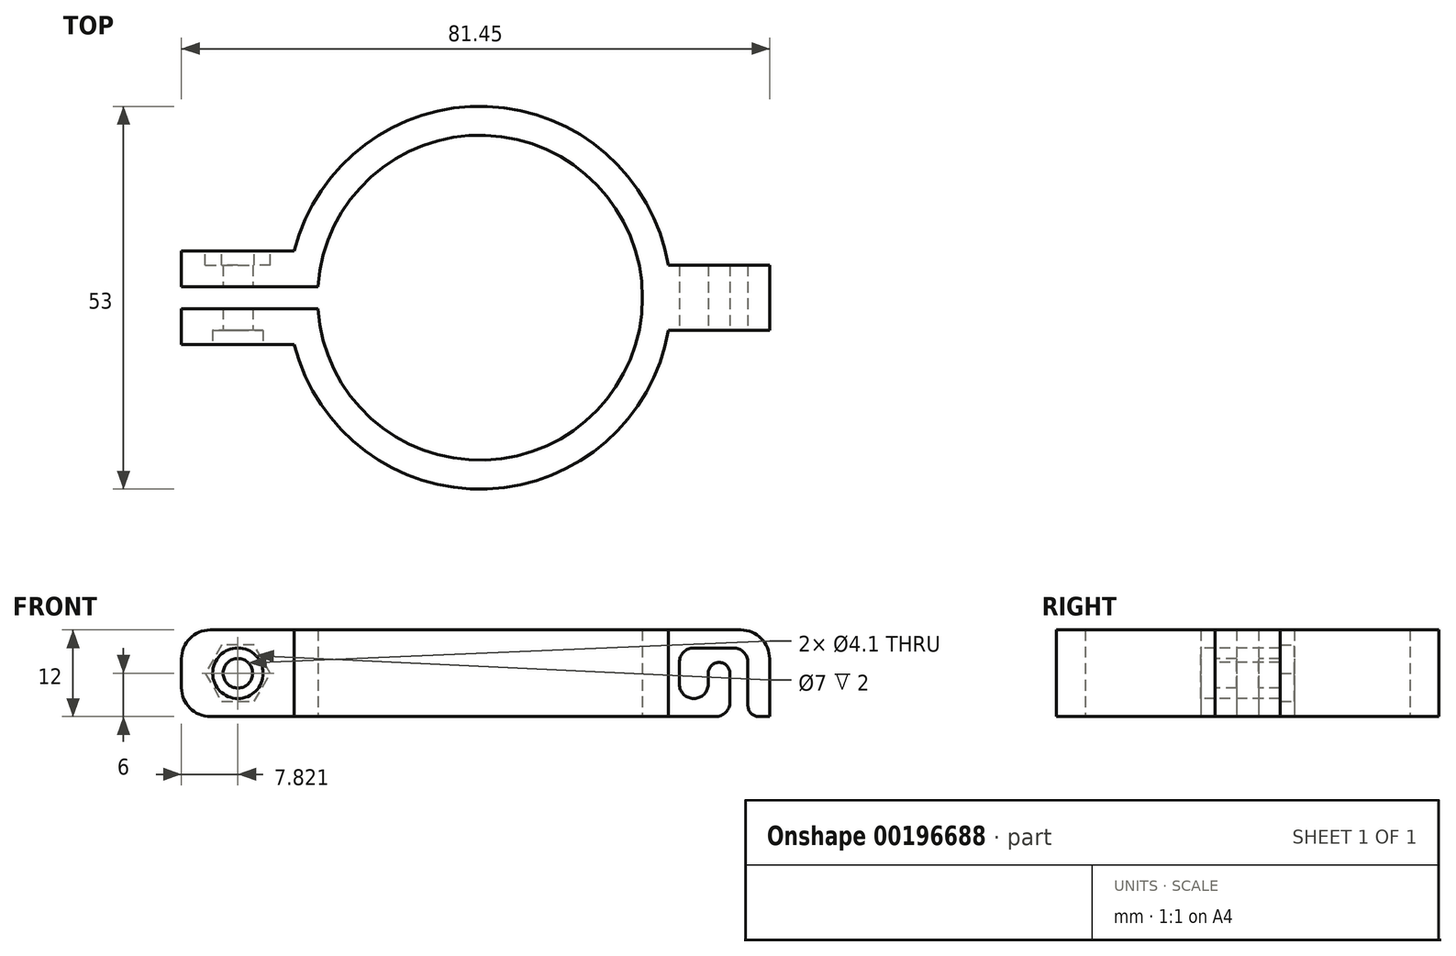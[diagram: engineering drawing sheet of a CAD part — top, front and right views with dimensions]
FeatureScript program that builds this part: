
annotation { "Feature Type Name" : "Feature", "Feature Type Description" : "" }
export const myFeature = defineFeature(function(context is Context, id is Id, definition is map)
    precondition{}
    {
        {
            var Q0;
            Q0=qCreatedBy(makeId("Top.planeOp"),FACE);
            var sketch = newSketch(context, id + "F0", { "sketchPlane" : qUnion([Q0])});
            skArc(sketch, "E0", {"start": v(-22.45, -1.5) * mm, "mid": v(22.5, 0) * mm, "end": v(-22.45, 1.5) * mm});
            skArc(sketch, "E1.0", {"start": v(-25.7, -6.5) * mm, "mid": v(1.02, -26.48) * mm, "end": v(26.12, -4.5) * mm});
            skLineSegment(sketch, "E2.top", {"start": v(-25.7, -6.5) * mm, "end": v(-41.33, -6.5) * mm});
            skLineSegment(sketch, "E2.right", {"start": v(-41.33, 6.5) * mm, "end": v(-41.33, 1.5) * mm});
            skLineSegment(sketch, "E3.MirrorCS", {"start": v(40.12, 4.5) * mm, "end": v(40.12, -4.5) * mm});
            skLineSegment(sketch, "E4", {"start": v(26.12, 4.5) * mm, "end": v(40.12, 4.5) * mm});
            skLineSegment(sketch, "E5", {"start": v(26.12, -4.5) * mm, "end": v(40.12, -4.5) * mm});
            skLineSegment(sketch, "E6", {"start": v(-22.45, 1.5) * mm, "end": v(-41.33, 1.5) * mm});
            skLineSegment(sketch, "E7", {"start": v(-22.45, -1.5) * mm, "end": v(-41.33, -1.5) * mm});
            skLineSegment(sketch, "E8.trimOffspring", {"start": v(-41.33, -1.5) * mm, "end": v(-41.33, -6.5) * mm});
            skLineSegment(sketch, "E9.trimOffspring", {"start": v(-25.7, 6.5) * mm, "end": v(-41.33, 6.5) * mm});
            skArc(sketch, "E10.trimOffspring", {"start": v(26.12, 4.5) * mm, "mid": v(1.02, 26.48) * mm, "end": v(-25.7, 6.5) * mm});
            skPoint(sketch, "E11", {"position": v(40.12, 0) * mm});
            skLineSegment(sketch, "E12", {"start": v(-65.67, 0) * mm, "end": v(55.66, 0) * mm, "construction": true});
            skSolve(sketch);
        }
        {
            var Q0;
            Q0=makeQuery(id+"F0.imprint","IMPRINT",FACE,{"disambiguationData":[TD([[makeQuery(id+"F0.imprint","IMPRINT",EDGE,{"derivedFrom":sQuery(id+"F0.wireOp",EDGE,"E0")}),-1.0]])]});
            extrude(context, id + "F1", {"entities" : qUnion([Q0]), "endBound" : BoundingType.SYMMETRIC, "depth" : 12 * mm});
        }
        {
            var Q0;
            Q0=makeQuery(id+"F1.opExtrude","SWEPT_FACE",FACE,{"disambiguationData":[OSD([sQuery(id+"F0.wireOp",EDGE,"E2.top")])]});
            var sketch = newSketch(context, id + "F2", { "sketchPlane" : qUnion([Q0])});
            skCircle(sketch, "E13", {"center": v(-33.5, 0) * mm, "radius": 2.05 * mm});
            skPoint(sketch, "E13.centerSnap0", {"position": v(-33.5, 6) * mm});
            skCircle(sketch, "E14", {"center": v(-33.5, 0) * mm, "radius": 3.5 * mm});
            skSolve(sketch);
        }
        {
            var Q0;
            Q0=makeQuery(id+"F1.opExtrude","SWEPT_FACE",FACE,{"disambiguationData":[OSD([sQuery(id+"F0.wireOp",EDGE,"E9.trimOffspring")])]});
            var sketch = newSketch(context, id + "F3", { "sketchPlane" : qUnion([Q0])});
            skCircle(sketch, "E15.cCircle", {"center": v(33.5, 0) * mm, "radius": 3.9 * mm, "construction": true});
            skPoint(sketch, "E15.cCircle.centerSnap0", {"position": v(33.5, -6) * mm});
            skPoint(sketch, "E15.cCircle.centerSnap1", {"position": v(41.33, 0) * mm});
            skLineSegment(sketch, "E15.0", {"start": v(35.76, -3.9) * mm, "end": v(31.26, -3.9) * mm});
            skLineSegment(sketch, "E15.1", {"start": v(31.26, -3.9) * mm, "end": v(29, 0) * mm});
            skLineSegment(sketch, "E15.2", {"start": v(29, 0) * mm, "end": v(31.26, 3.9) * mm});
            skLineSegment(sketch, "E15.3", {"start": v(31.26, 3.9) * mm, "end": v(35.76, 3.9) * mm});
            skLineSegment(sketch, "E15.4", {"start": v(35.76, 3.9) * mm, "end": v(38, 0) * mm});
            skLineSegment(sketch, "E15.5", {"start": v(38, 0) * mm, "end": v(35.76, -3.9) * mm});
            skPoint(sketch, "E15.0.midPoint", {"position": v(33.5, -3.9) * mm});
            skSolve(sketch);
        }
        {
            var Q0;
            Q0=makeQuery(id+"F1.opExtrude","SWEPT_FACE",FACE,{"disambiguationData":[OSD([sQuery(id+"F0.wireOp",EDGE,"E5")])]});
            var sketch = newSketch(context, id + "F4", { "sketchPlane" : qUnion([Q0])});
            skLineSegment(sketch, "E16", {"start": v(37.12, -4.5) * mm, "end": v(37.12, 1.5) * mm});
            skLineSegment(sketch, "E17", {"start": v(35.12, 3.5) * mm, "end": v(29.62, 3.5) * mm});
            skLineSegment(sketch, "E18", {"start": v(27.62, 1.5) * mm, "end": v(27.62, -1.5) * mm});
            skLineSegment(sketch, "E19", {"start": v(29.62, -3.5) * mm, "end": v(29.62, -3.5) * mm});
            skLineSegment(sketch, "E20", {"start": v(31.62, -1.5) * mm, "end": v(31.62, 0) * mm});
            skLineSegment(sketch, "E21", {"start": v(33.12, 1.5) * mm, "end": v(33.12, 1.5) * mm});
            skLineSegment(sketch, "E22", {"start": v(34.62, 0) * mm, "end": v(34.62, -4) * mm});
            skLineSegment(sketch, "E23", {"start": v(34.62, -6) * mm, "end": v(37.12, -6) * mm});
            skPoint(sketch, "E24.visualSharp", {"position": v(37.12, 3.5) * mm});
            skArc(sketch, "E24.filletArc", {"start": v(37.12, 1.5) * mm, "mid": v(36.53, 2.91) * mm, "end": v(35.12, 3.5) * mm});
            skPoint(sketch, "E25.visualSharp", {"position": v(31.62, -3.5) * mm});
            skArc(sketch, "E25.filletArc", {"start": v(29.62, -3.5) * mm, "mid": v(31.03, -2.91) * mm, "end": v(31.62, -1.5) * mm});
            skPoint(sketch, "E26.visualSharp", {"position": v(27.62, -3.5) * mm});
            skArc(sketch, "E26.filletArc", {"start": v(27.62, -1.5) * mm, "mid": v(28.2, -2.91) * mm, "end": v(29.62, -3.5) * mm});
            skPoint(sketch, "E27.visualSharp", {"position": v(27.62, 3.5) * mm});
            skArc(sketch, "E27.filletArc", {"start": v(29.62, 3.5) * mm, "mid": v(28.2, 2.91) * mm, "end": v(27.62, 1.5) * mm});
            skPoint(sketch, "E28.visualSharp", {"position": v(31.62, 1.5) * mm});
            skArc(sketch, "E28.filletArc", {"start": v(33.12, 1.5) * mm, "mid": v(32.05, 1.06) * mm, "end": v(31.62, 0) * mm});
            skPoint(sketch, "E29.visualSharp", {"position": v(34.62, 1.5) * mm});
            skArc(sketch, "E29.filletArc", {"start": v(34.62, 0) * mm, "mid": v(34.18, 1.06) * mm, "end": v(33.12, 1.5) * mm});
            skLineSegment(sketch, "E30", {"start": v(38.62, -6) * mm, "end": v(40.12, -6) * mm});
            skPoint(sketch, "E31.visualSharp", {"position": v(37.12, -6) * mm});
            skArc(sketch, "E31.filletArc", {"start": v(37.12, -4.5) * mm, "mid": v(37.55, -5.56) * mm, "end": v(38.62, -6) * mm});
            skLineSegment(sketch, "E32", {"start": v(32.62, -6) * mm, "end": v(26.12, -6) * mm});
            skPoint(sketch, "E33.visualSharp", {"position": v(34.62, -6) * mm});
            skArc(sketch, "E33.filletArc", {"start": v(32.62, -6) * mm, "mid": v(34.03, -5.41) * mm, "end": v(34.62, -4) * mm});
            skSolve(sketch);
        }
        {
            var Q0;
            Q0=makeQuery(id+"F4.imprint","IMPRINT",FACE,{"disambiguationData":[TD([[makeQuery(id+"F4.imprint","IMPRINT",EDGE,{"derivedFrom":sQuery(id+"F4.wireOp",EDGE,"E16")}),1.0]])]});
            var Q1;
            Q1=makeQuery(id+"F1.opExtrude","SWEPT_FACE",FACE,{"disambiguationData":[OSD([sQuery(id+"F0.wireOp",EDGE,"E4")])]});
            extrude(context, id + "F5", {"entities" : qUnion([Q0]), "operationType" : NewBodyOperationType.REMOVE, "endBound" : BoundingType.UP_TO_SURFACE, "oppositeDirection" : true, "endBoundEntityFace" : qUnion([Q1]), "depth" : 25 * mm});
        }
        {
            var Q0;
            Q0=makeQuery(id+"F2.imprint","IMPRINT",FACE,{"disambiguationData":[TD([[makeQuery(id+"F2.imprint","IMPRINT",EDGE,{"derivedFrom":sQuery(id+"F2.wireOp",EDGE,"E13")}),1.0]])]});
            var Q1;
            Q1=makeQuery(id+"F1.opExtrude","SWEPT_FACE",FACE,{"disambiguationData":[OSD([sQuery(id+"F0.wireOp",EDGE,"E9.trimOffspring")])]});
            extrude(context, id + "F6", {"entities" : qUnion([Q0]), "operationType" : NewBodyOperationType.REMOVE, "endBound" : BoundingType.UP_TO_SURFACE, "oppositeDirection" : true, "endBoundEntityFace" : qUnion([Q1]), "depth" : 25 * mm});
        }
        {
            var Q0;
            Q0=makeQuery(id+"F2.imprint","IMPRINT",FACE,{"disambiguationData":[TD([[makeQuery(id+"F2.imprint","IMPRINT",EDGE,{"derivedFrom":sQuery(id+"F2.wireOp",EDGE,"E13")}),-1.0]])]});
            extrude(context, id + "F7", {"entities" : qUnion([Q0]), "operationType" : NewBodyOperationType.REMOVE, "oppositeDirection" : true, "depth" : 2 * mm});
        }
        {
            var Q0;
            Q0=makeQuery(id+"F3.imprint","IMPRINT",FACE,{"disambiguationData":[TD([[makeQuery(id+"F3.imprint","IMPRINT",EDGE,{"derivedFrom":sQuery(id+"F3.wireOp",EDGE,"E15.0")}),-1.0]])]});
            extrude(context, id + "F8", {"entities" : qUnion([Q0]), "operationType" : NewBodyOperationType.REMOVE, "oppositeDirection" : true, "depth" : 2 * mm});
        }
        {
            var Q0;
            Q0=makeQuery(id+"F1.opExtrude","CAP_EDGE",EDGE,{"disambiguationData":[OSD([sQuery(id+"F0.wireOp",EDGE,"E8.trimOffspring")])],"isStart":false});
            var Q1;
            Q1=makeQuery(id+"F1.opExtrude","CAP_EDGE",EDGE,{"disambiguationData":[OSD([sQuery(id+"F0.wireOp",EDGE,"E2.right")])],"isStart":false});
            var Q2;
            Q2=makeQuery(id+"F1.opExtrude","CAP_EDGE",EDGE,{"disambiguationData":[OSD([sQuery(id+"F0.wireOp",EDGE,"E2.right")])],"isStart":true});
            var Q3;
            Q3=makeQuery(id+"F1.opExtrude","CAP_EDGE",EDGE,{"disambiguationData":[OSD([sQuery(id+"F0.wireOp",EDGE,"E8.trimOffspring")])],"isStart":true});
            var Q4;
            Q4=makeQuery(id+"F1.opExtrude","CAP_EDGE",EDGE,{"disambiguationData":[OSD([sQuery(id+"F0.wireOp",EDGE,"E3.MirrorCS")])],"isStart":false});
            fillet(context, id + "F9", {"entities" : qUnion([Q0, Q1, Q2, Q3, Q4]), "radius" : 4 * mm, "tangentPropagation" : true, "allowEdgeOverflow" : false});
        }
    });
